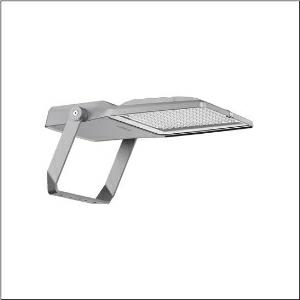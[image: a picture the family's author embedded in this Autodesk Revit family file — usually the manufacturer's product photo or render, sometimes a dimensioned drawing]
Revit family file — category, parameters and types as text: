
# Revit family: floodlight_fl_21_iq_midi___rs12_5xa7781e2b1a_85c8
name_source: partatom
category: Lighting Fixtures
units: mm (PartAtom-declared; Revit-internal decimal feet)

## family parameters
Cut with Voids When Loaded = No
Host = Face
Light Source = No
Part Type = Normal
Room Calculation Point = No
Round Connector Dimension = Use Diameter
Shared = No

## types (1)
- --- (1 x LED, 26730 lm, 208.1 W, 3000K)
    Apparent Load = 208 VA
    CIE Flux Codes = 79 92 99 100 100
    Color Rendering = 70
    Color Temperature = 3000K
    Default Elevation = 1800 mm
    Description = Floodlight FL 21 iQ midi, floodlight, primary light control with lens, of PMMA, primary optical cover: protective disc, of toughened safety glass, transparent, light distribution: RS12, light emission: direct distribution, installation type: surface-mounted, LED, High Power LED, rated luminous flux: 26.730lm, luminous efficacy: 128lm/W, light colour: 730, colour temperature: 3000K, control gear: iQ Comfort/DALI, control: optimised constant luminous flux control (CLO 2.0), Desk-Remote (wireless, voltage-free reading and setting of iQ features in the workshop via application-optimized NFC function/RFID function), Light-Fading, Smart-Wire, Night-Set, Lumen-Switch, Temp-Guard, Auto-Match, with terminal, 6-pole, mains connection: 220..240V, AC, 50/60Hz, start of lifetime: 208W, end of service life: 227W, reduction: 90W, luminaire housing, of diecast aluminium, powder-coated, Siteco® metallic grey (DB 702S), corrosivity category C5 mid according to DIN EN ISO 12944, suitable for swimming pools, chlorine-resistant, sealing non-destructively replaceable, mounting bracket, of steel, galvanised, powder-coated, Siteco® metallic grey (DB 702S), protection rating (complete): IP66, insulation class (complete): insulation class II (safety insulation), certification: CE, ENEC, VDE, protection symbol: D, impact resistance: IK08, permissible operating ambient temperature: -40..+40°C, permissible operating ambient temperature for outdoor applications: -40..+50°C, standard: DIN EN 12944, LABS conformity tested according to VDMA 24364:2018-05, packaging unit: 1 piece

Light Distribution: RS12
    Height = 76 mm
    Lamp = 1 x LED
    Lamp Light Flux = 26730 lm
    Lamp Power = 208.1 W
    Lamp count = 1
    Length = 657 mm
    Luminous efficacy = 128 lm/W
    Manufacturer = Siteco
    ModVariant = No
    Model = 5XA7781E2B1A
    Number of Poles = 1
    OnlyDefault = Yes
    Power Factor = 1
    Product Name = Floodlight FL 21 iQ midi | RS12
    Product group = floodlight | pylon annexe
    ProductGroupID = 6200
    Protection Class = Protection class II
    Protection Degree = IP 66
    RLX_Detail_Level = 1
    RLX_Emergency_Light_Flux = 0 lm
    RLX_Emergency_Type = 0
    RLX_Emergency_Type_DB = No
    RlxData = <blob elided: 141201 chars, md5=7d85e744>
    Socket = socket
    Standby Power = 0 W
    System Light Flux = 26730 lm
    System Power = 208 W
    Type Comments = factory setting: luminous flux: 100 % | dim-lin: 254 | 710 mA
    Type Image = l_1006876.jpg
    URL = http://relux.com
    VarID = @adj_107932
    Voltage = 0 V
    Weight = 0.00 kg
    Width = 442 mm

## geometry (parser evidence)
native form markers: Blend x4, Sweep x12
no freeform markers — native parametric forms only
